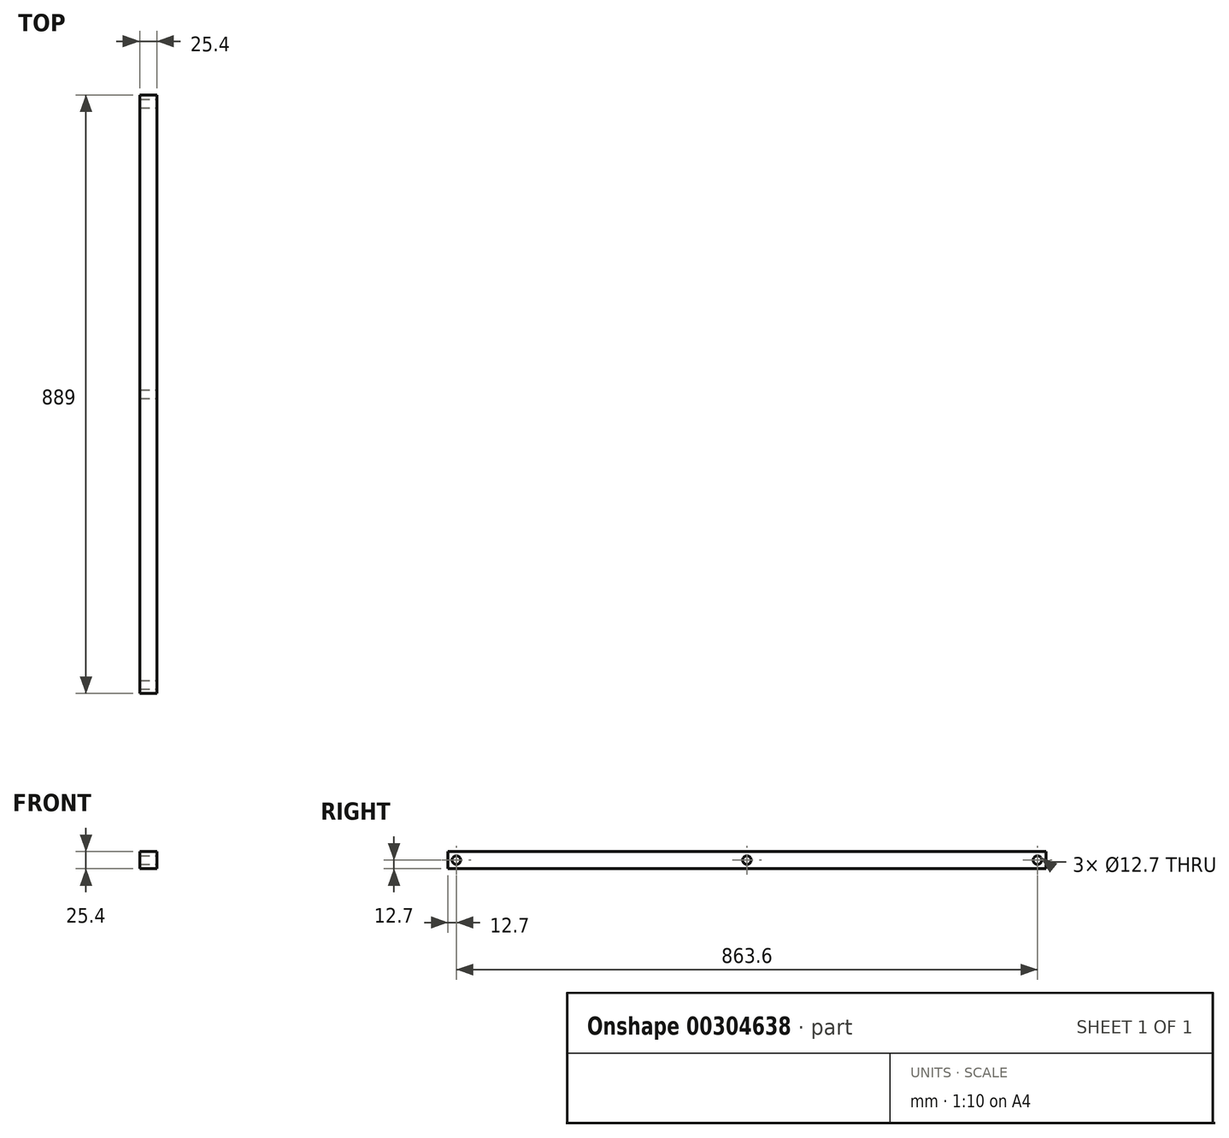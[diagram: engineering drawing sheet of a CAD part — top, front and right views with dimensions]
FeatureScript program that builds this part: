
annotation { "Feature Type Name" : "Feature", "Feature Type Description" : "" }
export const myFeature = defineFeature(function(context is Context, id is Id, definition is map)
    precondition{}
    {
        {
            var Q0;
            Q0=qCreatedBy(makeId("Front.planeOp"),FACE);
            var sketch = newSketch(context, id + "F0", { "sketchPlane" : qUnion([Q0])});
            skLineSegment(sketch, "E0.bottom", {"start": v(12.7, 12.7) * mm, "end": v(-12.7, 12.7) * mm});
            skLineSegment(sketch, "E0.top", {"start": v(12.7, -12.7) * mm, "end": v(-12.7, -12.7) * mm});
            skLineSegment(sketch, "E0.left", {"start": v(12.7, 12.7) * mm, "end": v(12.7, -12.7) * mm});
            skLineSegment(sketch, "E0.right", {"start": v(-12.7, 12.7) * mm, "end": v(-12.7, -12.7) * mm});
            skPoint(sketch, "E0.middle", {"position": v(0, 0) * mm});
            skSolve(sketch);
        }
        {
            var Q0;
            Q0 = qSketchRegion(id + "F0", true);
            extrude(context, id + "F1", {"entities" : qUnion([Q0]), "endBound" : BoundingType.SYMMETRIC, "depth" : 889 * mm});
        }
        {
            var Q0;
            Q0=makeQuery(id+"F1.opExtrude","SWEPT_FACE",FACE,{"disambiguationData":[OSD([sQuery(id+"F0.wireOp",EDGE,"E0.left")])]});
            var sketch = newSketch(context, id + "F2", { "sketchPlane" : qUnion([Q0])});
            skCircle(sketch, "E1", {"center": v(-431.8, 0) * mm, "radius": 6.35 * mm});
            skCircle(sketch, "E2", {"center": v(431.8, 0) * mm, "radius": 6.35 * mm});
            skSolve(sketch);
        }
        {
            var Q0;
            Q0 = qSketchRegion(id + "F2", true);
            extrude(context, id + "F3", {"entities" : qUnion([Q0]), "operationType" : NewBodyOperationType.REMOVE, "endBound" : BoundingType.THROUGH_ALL, "oppositeDirection" : true, "depth" : 25.4 * mm});
        }
        {
            var Q0;
            Q0=makeQuery(id+"F1.opExtrude","SWEPT_FACE",FACE,{"disambiguationData":[OSD([sQuery(id+"F0.wireOp",EDGE,"E0.left")])]});
            var sketch = newSketch(context, id + "F4", { "sketchPlane" : qUnion([Q0])});
            skCircle(sketch, "E3", {"center": v(0, 0) * mm, "radius": 6.35 * mm});
            skSolve(sketch);
        }
        {
            var Q0;
            Q0 = qSketchRegion(id + "F4", true);
            extrude(context, id + "F5", {"entities" : qUnion([Q0]), "operationType" : NewBodyOperationType.REMOVE, "endBound" : BoundingType.THROUGH_ALL, "oppositeDirection" : true, "depth" : 25.4 * mm});
        }
    });
